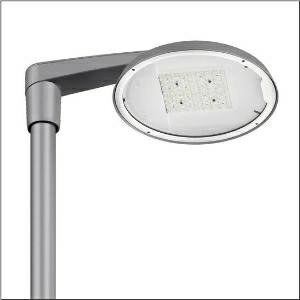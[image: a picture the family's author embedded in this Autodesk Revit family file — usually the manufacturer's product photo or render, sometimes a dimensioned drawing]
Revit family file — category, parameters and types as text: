
# Revit family: dl_r__50_iq_mini___st0_5a_5xa248b31f08le_a236
name_source: partatom
category: Lighting Fixtures
units: mm (PartAtom-declared; Revit-internal decimal feet)

## family parameters
Cut with Voids When Loaded = No
Host = Face
Light Source = No
Part Type = Normal
Room Calculation Point = No
Round Connector Dimension = Use Diameter
Shared = No

## types (1)
- --- (1 x LED, 10390 lm, 67.4 W, 3000K)
    Apparent Load = 67 VA
    CIE Flux Codes = 41 75 97 100 100
    Color Rendering = 70
    Color Temperature = 3000K
    Default Elevation = 1800 mm
    Description = DL® 50 iQ mini, mast luminaire, primary light control with lens, of PMMA, primary optical cover: cover, of toughened safety glass, transparent, light distribution: ST0.5a, light emission: direct distribution, primary light characteristic: asymmetric, installation type: side-entry, post-top, LED, High Power LED, rated luminous flux: 10.390lm, luminous efficacy: 154lm/W, light colour: 730, colour temperature: 3000K, control gear: iQ Street-Remote, control: optimised constant luminous flux control (CLO 2.0), Desk-Remote (wireless, voltage-free reading and setting of iQ features in the workshop via application-optimized NFC function/RFID function), Light-Fading, Smart-Wire, Night-Set, Lumen-Switch, Temp-Guard, Auto-Match, Street-Remote, mains connection: 230..240V, AC, 50/60Hz, connection cable pre-assembled, cable length: 8,5m, start of lifetime: 67W, end of service life: 70W, reduction: 31W, luminaire housing, of diecast aluminium, powder-coated, Siteco® metallic grey (DB 702S), inclination adjustable: 0°, 5°, 10° (post-top) | 0°, -5°, -10°, -15° (side-entry), please order mast post-top element or mast side-entry element separately, diameter: 500mm, height: 115mm, post-top: for spigot size d x l = 76 x 100mm; with reducer (optional accessory) 60 x 100mm | side-entry: for spigot size d x l = 60 x 100mm; with reducer (optional accessory) 42 x 100mm, mounting height: 4..6m, protection rating (complete): IP66, insulation class (complete): insulation class II (safety insulation), certification: CE, ENEC, ENEC+, VDE, impact resistance: IK08, permissible operating ambient temperature for outdoor applications: -25..+40°C, standard-compliant lighting for roads and squares, packaging unit: 1 piece

Light Distribution: ST0.5a
    Height = 115 mm
    Lamp = 1 x LED
    Lamp Light Flux = 10390 lm
    Lamp Power = 67.4 W
    Lamp count = 1
    Length = 500 mm
    Luminous efficacy = 154 lm/W
    Manufacturer = Siteco
    ModVariant = No
    Model = 5XA248B31F08LE
    Number of Poles = 1
    OnlyDefault = Yes
    Power Factor = 1
    Product Name = DL® 50 iQ mini | ST0.5a
    Product group = mast luminaire | pylon top
    ProductGroupID = 6100
    Protection Class = Protection class II
    Protection Degree = IP 66
    RLX_Detail_Level = 1
    RLX_Emergency_Light_Flux = 0 lm
    RLX_Emergency_Type = 0
    RLX_Emergency_Type_DB = No
    RlxData = <blob elided: 127965 chars, md5=d3044b97>
    Socket = socket
    Standby Power = 0 W
    System Light Flux = 10390 lm
    System Power = 67 W
    Type Comments = factory setting: luminous flux: 100 % | dim-lin: 254 | 705 mA
    Type Image = l_1251790.jpg
    URL = http://relux.com
    VarID = @adj_164627
    Voltage = 0 V
    Weight = 0.00 kg
    Width = 0 mm  [stored 0 ft]

note: [stored X ft] marks values corroborated as IEEE doubles in the binary element streams (Revit-internal decimal feet)

## geometry (parser evidence)
native form markers: Blend x4, Sweep x12
no freeform markers — native parametric forms only
